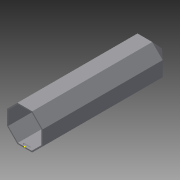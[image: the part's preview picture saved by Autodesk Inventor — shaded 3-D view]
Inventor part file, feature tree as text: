
AUTODESK INVENTOR PART (.ipt)
format: ipt  version: 2015 SP2 (Build 190223200, 223)  size: 189,440 bytes
history: native  units: mm
features: extrude x3, sketch x3, chamfer x2, plane x1, loft x1, shell x1, other x1
ambient origin geometry x8: Origin, YZ Plane, XZ Plane, XY Plane, X Axis, Y Axis, Z Axis, Center Point
bodies: Solid1 (feature_tree)
feature tree (12):
  extrude  "Extrusion1"  Depth=175.0mm TaperAngle=0.0deg
  plane  "Work Plane1"
  loft  "Loft1"
  shell  "Shell2"  Thickness=20.0mm
  sketch  "Sketch8"  dims[d7=0.0mm d8=90.0deg d9=0.0mm d10=90.0deg d13=1.75mm d14=10.0mm d15=2.5mm d16=2.0mm d17=10.0mm d18=2.5mm d19=3.25mm d20=1.0mm d21=0.0mm d22=1.0mm d23=0.0mm d24=1.0mm d25=2.0mm d26=6.108652mm d27=1.0mm d28=2.0mm d29=6.108652mm]
  extrude  "Extrusion2"  TaperAngle=0.0deg  [1 undecoded]
  extrude  "Extrusion3"  Depth=1.0mm
  chamfer  "Chamfer1"  Distance=10.0mm
  chamfer  "Chamfer2"  Distance=2.5mm
  sketch  "Sketch1"  dims[d0=52.0mm d1=175.0mm d2=0.0mm]
  sketch  "Sketch2"  dims[d4=15.0mm d5=20.0mm d6=20.0mm]
  other  "Edges1"
note: 1 required parameter value undecoded (feature->parameter linkage not recoverable at this tier; creation-order binding heuristic only, values carry confidence <= 0.55)
